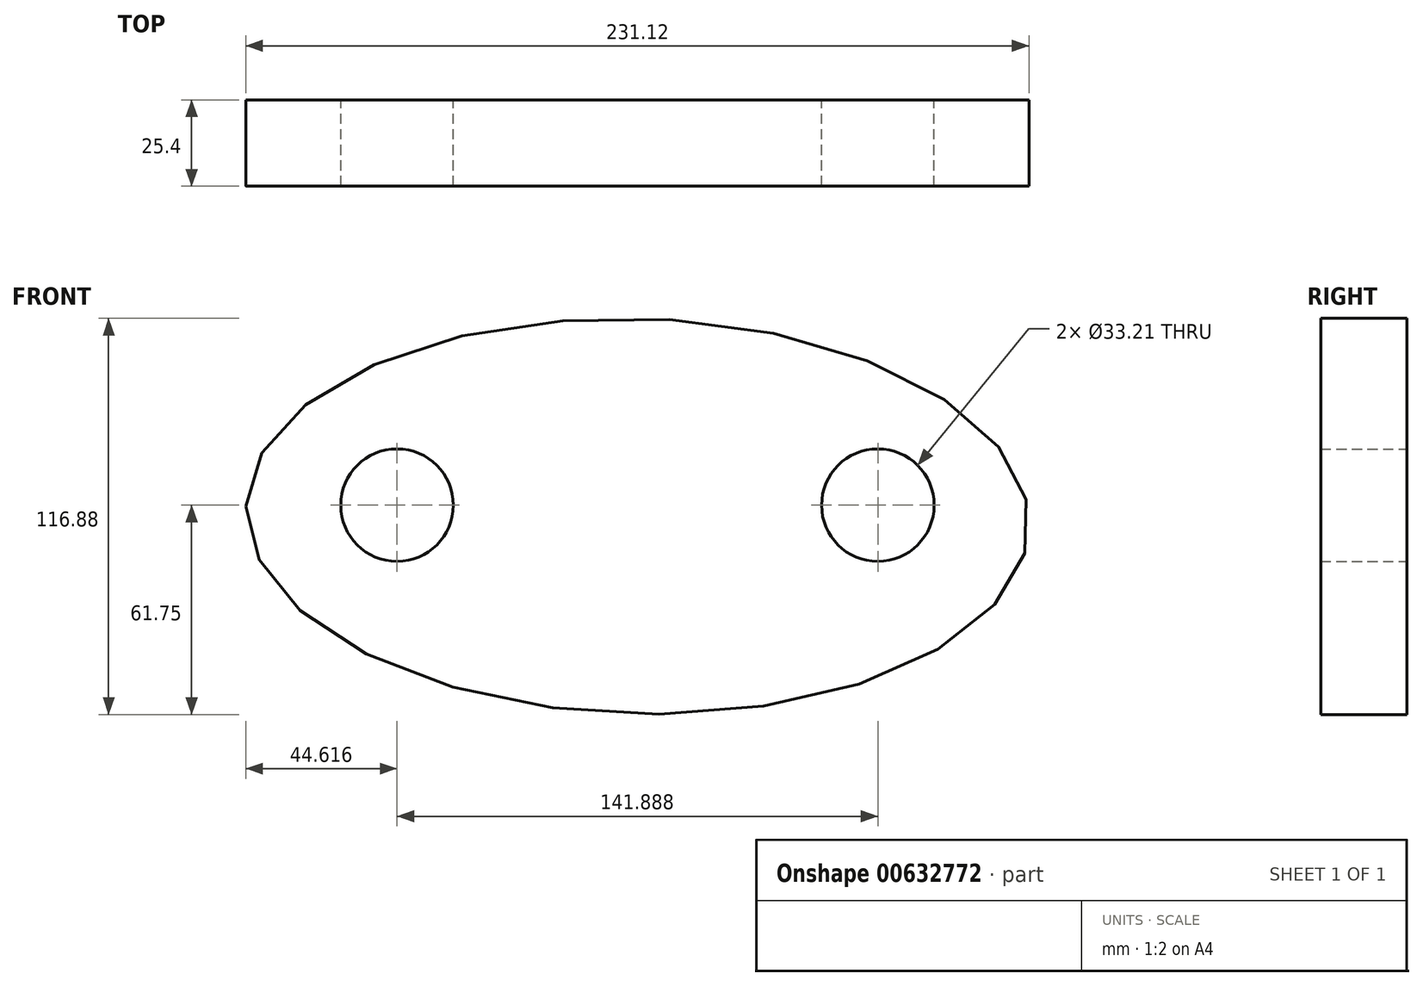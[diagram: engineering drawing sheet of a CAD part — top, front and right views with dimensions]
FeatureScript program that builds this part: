
annotation { "Feature Type Name" : "Feature", "Feature Type Description" : "" }
export const myFeature = defineFeature(function(context is Context, id is Id, definition is map)
    precondition{}
    {
        {
            var Q0;
            Q0=qCreatedBy(makeId("Front.planeOp"),FACE);
            var sketch = newSketch(context, id + "F0", { "sketchPlane" : qUnion([Q0])});
            skEllipse(sketch, "E0", {"center": v(0, 0) * mm, "majorRadius": 115.6 * mm, "minorRadius": 58.38 * mm, "majorAxis": v(-1, 0.03)});
            skCircle(sketch, "E1", {"center": v(-70.94, 3.3) * mm, "radius": 16.6 * mm});
            skCircle(sketch, "E2.MirrorC", {"center": v(70.94, 3.3) * mm, "radius": 16.6 * mm});
            skSolve(sketch);
        }
        {
            var Q0;
            Q0 = qSketchRegion(id + "F0", true);
            extrude(context, id + "F1", {"entities" : qUnion([Q0]), "depth" : 25.4 * mm, "offsetDistance" : 25.4 * mm});
        }
    });
